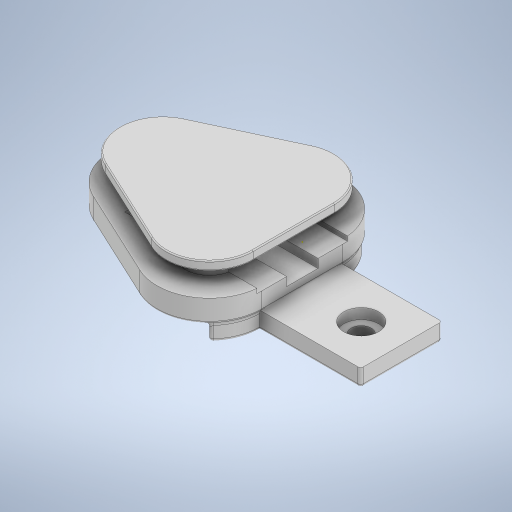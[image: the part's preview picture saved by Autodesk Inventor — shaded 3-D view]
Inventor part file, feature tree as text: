
AUTODESK INVENTOR PART (.ipt)
format: ipt  version: 2024.3 (Build 283343000, 343)  size: 480,256 bytes
history: native  units: in
note: dims shown in document units (in); Inventor stores cm internally (conversion verified against a paired STEP export)
features: sketch x10, extrude x9, fillet x5, projected_geometry x4
ambient origin geometry x8: Origin, YZ Plane, XZ Plane, XY Plane, X Axis, Y Axis, Z Axis, Center Point
bodies: Solid1 (feature_tree)
feature tree (28):
  extrude  "Extrusion1"  Depth=1.9685in
  extrude  "Extrusion2"  Depth=1.9685in
  extrude  "Extrusion3"  Depth=1.1024in
  sketch  "Sketch4"  dims[d7=0.3937in d8=0.0in d9=2.3622in]
  extrude  "Extrusion4"  Depth=0.3937in
  extrude  "Extrusion5"  Depth=0.1969in
  fillet  "Fillet1"  Radius=2.0472in
  fillet  "Fillet2"  Radius=2.9921in
  extrude  "Extrusion6"  Depth=0.7087in
  extrude  "Extrusion7"  Depth=0.0236in
  extrude  "Extrusion8"  TaperAngle=45.0deg  [1 undecoded]
  extrude  "Extrusion9"  Depth=0.3937in TaperAngle=0.0deg
  fillet  "Fillet3"  Radius=0.7874in
  fillet  "Fillet4"  Radius=0.9055in
  fillet  "Fillet5"  Radius=0.2362in
  sketch  "Sketch1"  dims[d0=0.3436in d1=1.9685in]
  sketch  "Sketch2"  dims[d2=2.9528in d3=1.9685in]
  projected_geometry  "Projected Loop1"
  sketch  "Sketch3"  dims[d4=0.1969in d5=0.0in d6=1.1024in]
  projected_geometry  "Projected Loop2"
  sketch  "Sketch5"  dims[d10=0.5in d11=0.0in d12=0.1969in d13=2.0472in d14=2.9921in d15=0.0in]
  sketch  "Sketch6"  dims[d16=0.1969in d17=0.7087in]
  sketch  "Sketch7"  dims[d18=0.9843in d19=0.0in d20=0.0236in]
  projected_geometry  "Projected Loop3"
  sketch  "Sketch8"  dims[d21=0.0472in d22=45.0deg]
  sketch  "Sketch9"  dims[d23=2.2835in d24=0.3937in d25=0.0in d26=0.7874in d27=0.9055in d28=0.2362in d29=0.0in]
  projected_geometry  "Projected Loop4"
  sketch  "Sketch10"  dims[d30=0.5512in d31=0.5in d32=0.0in d33=0.4528in d34=0.0in d35=0.0in d36=0.063in d37=0.063in d38=0.1181in]
note: 1 required parameter value undecoded (feature->parameter linkage not recoverable at this tier; creation-order binding heuristic only, values carry confidence <= 0.55)
